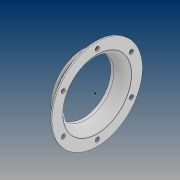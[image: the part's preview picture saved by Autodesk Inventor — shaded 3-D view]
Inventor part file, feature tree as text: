
AUTODESK INVENTOR PART (.ipt)
format: ipt  version: 2021 (Build 250183000, 183)  size: 359,936 bytes
history: native  units: mm
features: thread x9, sketch x5, fillet x4, extrude x2, revolve x2, pattern_circular x1
ambient origin geometry x8: Origin, YZ Plane, XZ Plane, XY Plane, X Axis, Y Axis, Z Axis, Center Point
bodies: Solid1 (feature_tree)
feature tree (23):
  extrude  "Extrusion1"  Depth=465.0mm
  revolve  "Revolution1"  [1 undecoded]
  sketch  "Sketch4"  dims[d8=10.0mm d9=0.0mm d10=90.0deg]
  extrude  "Extrusion3"  TaperAngle=90.0deg  [1 undecoded]
  revolve  "Revolution2"  [1 undecoded]
  thread  "Thread1"  [1 undecoded]
  pattern_circular  "Circular Pattern1"  [2 undecoded]
  thread  "Thread2"  [1 undecoded]
  thread  "Thread3"  [1 undecoded]
  thread  "Thread4"  [1 undecoded]
  thread  "Thread5"  [1 undecoded]
  thread  "Thread6"  [1 undecoded]
  thread  "Thread7"  [1 undecoded]
  thread  "Thread8"  [1 undecoded]
  thread  "Thread9"  [1 undecoded]
  fillet  "Fillet2"  Radius=10.0mm
  fillet  "Fillet3"  Radius=163.918888mm
  fillet  "Fillet4"  Radius=188.918888mm
  fillet  "Fillet5"  Radius=4.0mm
  sketch  "Sketch1"  dims[d0=536.0mm d1=465.0mm]
  sketch  "Sketch2"  dims[d2=406.5mm d3=25.0mm]
  sketch  "Sketch5"  dims[d15=353.0mm d16=10.0mm d17=10.0mm d18=0.0mm]
  sketch  "Sketch6"  dims[d19=90.0deg d20=10.0mm d21=0.0mm d22=80.0mm d23=360.0deg d25=10.0mm d26=0.0mm d27=10.0mm d28=0.0mm d29=10.0mm d30=0.0mm d31=10.0mm d32=0.0mm d33=10.0mm d34=0.0mm d35=10.0mm d36=0.0mm d37=10.0mm d38=0.0mm d39=10.0mm d40=0.0mm d43=163.918888mm d44=188.918888mm d46=4.0mm d47=4.0mm d48=2.0mm d49=2.0mm d50=60.0mm d52=360.0deg]
note: 14 required parameter values undecoded (feature->parameter linkage not recoverable at this tier; creation-order binding heuristic only, values carry confidence <= 0.55)